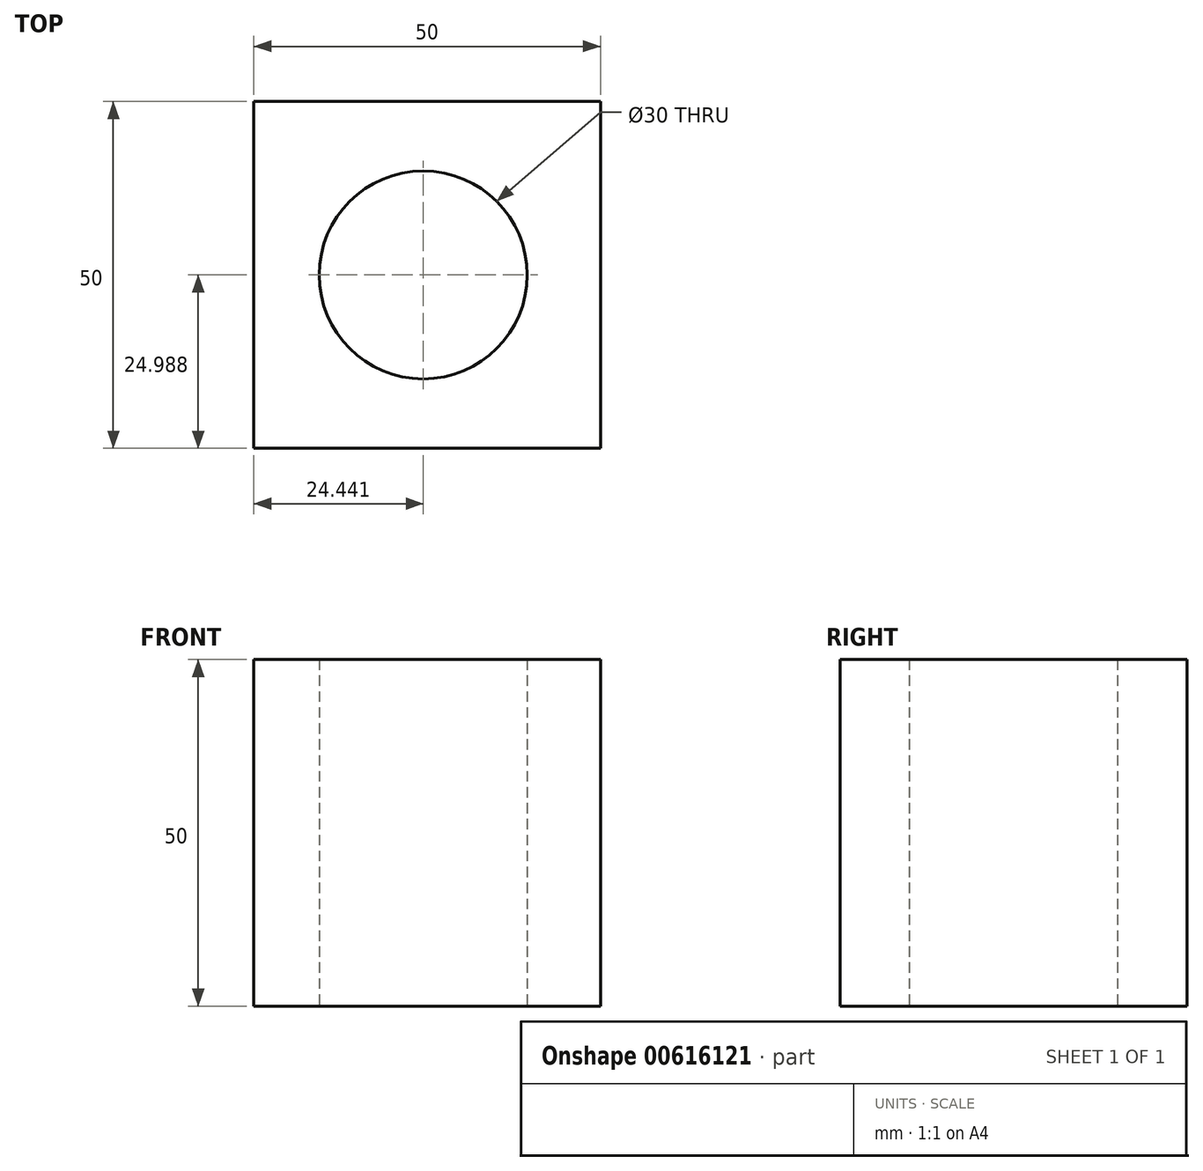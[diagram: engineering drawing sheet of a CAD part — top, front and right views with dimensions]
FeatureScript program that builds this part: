
annotation { "Feature Type Name" : "Feature", "Feature Type Description" : "" }
export const myFeature = defineFeature(function(context is Context, id is Id, definition is map)
    precondition{}
    {
        {
            var Q0;
            Q0=qCreatedBy(makeId("Top.planeOp"),FACE);
            var sketch = newSketch(context, id + "F0", { "sketchPlane" : qUnion([Q0])});
            skLineSegment(sketch, "E0.bottom", {"start": v(0, 0) * mm, "end": v(-50, 0) * mm});
            skLineSegment(sketch, "E0.top", {"start": v(0, 50) * mm, "end": v(-50, 50) * mm});
            skLineSegment(sketch, "E0.left", {"start": v(0, 0) * mm, "end": v(0, 50) * mm});
            skLineSegment(sketch, "E0.right", {"start": v(-50, 0) * mm, "end": v(-50, 50) * mm});
            skSolve(sketch);
        }
        {
            var Q0;
            Q0 = qSketchRegion(id + "F0", true);
            extrude(context, id + "F1", {"entities" : qUnion([Q0]), "depth" : 50 * mm, "offsetDistance" : 25 * mm});
        }
        {
            var Q0;
            Q0=qCreatedBy(makeId("Top.planeOp"),FACE);
            var sketch = newSketch(context, id + "F2", { "sketchPlane" : qUnion([Q0])});
            skCircle(sketch, "E1", {"center": v(-25.56, 24.99) * mm, "radius": 15 * mm});
            skSolve(sketch);
        }
        {
            var Q0;
            Q0 = qSketchRegion(id + "F2", true);
            extrude(context, id + "F3", {"entities" : qUnion([Q0]), "operationType" : NewBodyOperationType.REMOVE, "depth" : 50 * mm, "offsetDistance" : 25 * mm});
        }
    });
